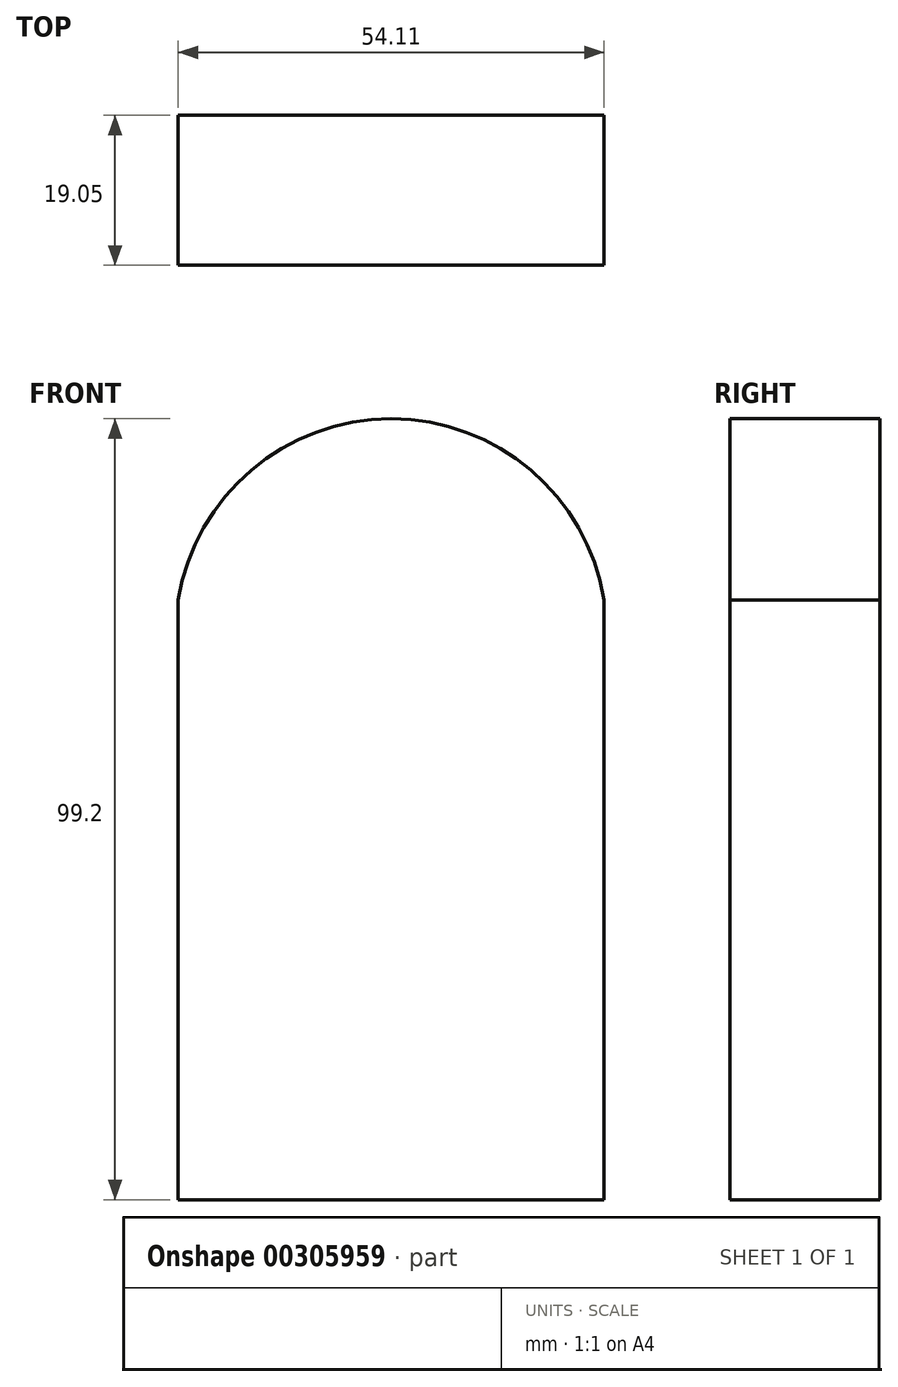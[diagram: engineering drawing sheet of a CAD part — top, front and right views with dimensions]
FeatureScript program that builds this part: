
annotation { "Feature Type Name" : "Feature", "Feature Type Description" : "" }
export const myFeature = defineFeature(function(context is Context, id is Id, definition is map)
    precondition{}
    {
        {
            var Q0;
            Q0=qCreatedBy(makeId("Front.planeOp"),FACE);
            var sketch = newSketch(context, id + "F0", { "sketchPlane" : qUnion([Q0])});
            skLineSegment(sketch, "E0", {"start": v(-38.28, 28.78) * mm, "end": v(-38.28, -47.42) * mm});
            skLineSegment(sketch, "E1", {"start": v(-38.28, -47.42) * mm, "end": v(15.83, -47.42) * mm});
            skLineSegment(sketch, "E2", {"start": v(15.83, -47.42) * mm, "end": v(15.83, 28.78) * mm});
            skArc(sketch, "E3", {"start": v(15.83, 28.78) * mm, "mid": v(-11.22, 51.78) * mm, "end": v(-38.28, 28.78) * mm});
            skSolve(sketch);
        }
        {
            var Q0;
            Q0 = qSketchRegion(id + "F0", true);
            extrude(context, id + "F1", {"entities" : qUnion([Q0]), "depth" : 19.05 * mm});
        }
    });
